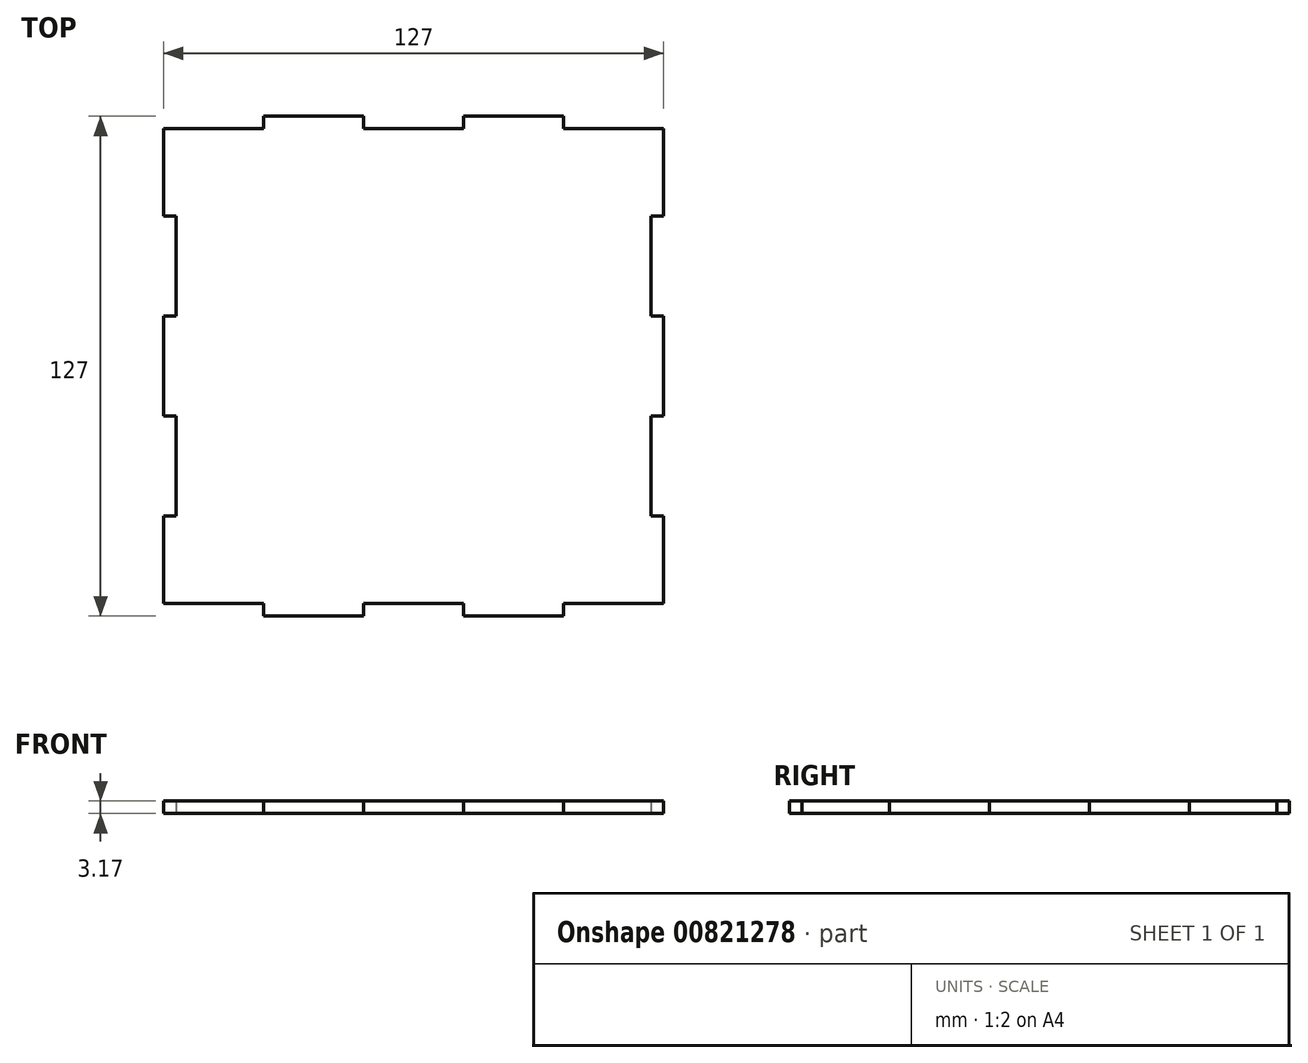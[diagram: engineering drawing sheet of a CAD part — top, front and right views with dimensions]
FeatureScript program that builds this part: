
annotation { "Feature Type Name" : "Feature", "Feature Type Description" : "" }
export const myFeature = defineFeature(function(context is Context, id is Id, definition is map)
    precondition{}
    {
        {
            var Q0;
            Q0=qCreatedBy(makeId("Top.planeOp"),FACE);
            var sketch = newSketch(context, id + "F0", { "sketchPlane" : qUnion([Q0])});
            skLineSegment(sketch, "E0.bottom", {"start": v(-63.5, 63.5) * mm, "end": v(63.5, 63.5) * mm});
            skLineSegment(sketch, "E0.top", {"start": v(-63.5, -63.5) * mm, "end": v(63.5, -63.5) * mm});
            skLineSegment(sketch, "E0.left", {"start": v(-63.5, 63.5) * mm, "end": v(-63.5, -63.5) * mm});
            skLineSegment(sketch, "E0.right", {"start": v(63.5, 63.5) * mm, "end": v(63.5, -63.5) * mm});
            skPoint(sketch, "E0.middle", {"position": v(0, 0) * mm});
            skLineSegment(sketch, "E1", {"start": v(-38.1, 63.5) * mm, "end": v(-38.1, -63.5) * mm});
            skLineSegment(sketch, "E2", {"start": v(-63.5, -38.1) * mm, "end": v(63.5, -38.1) * mm});
            skLineSegment(sketch, "E3.1.0.0", {"start": v(-12.7, 63.5) * mm, "end": v(-12.7, -63.5) * mm});
            skLineSegment(sketch, "E3.2.0.0", {"start": v(12.7, 63.5) * mm, "end": v(12.7, -63.5) * mm});
            skLineSegment(sketch, "E3.3.0.0", {"start": v(38.1, 63.5) * mm, "end": v(38.1, -63.5) * mm});
            skLineSegment(sketch, "E3.direction1", {"start": v(-38.1, -63.5) * mm, "end": v(-12.7, -63.5) * mm, "construction": true});
            skLineSegment(sketch, "E4.0.1.0", {"start": v(-63.5, -12.7) * mm, "end": v(63.5, -12.7) * mm});
            skLineSegment(sketch, "E4.0.2.0", {"start": v(-63.5, 12.7) * mm, "end": v(63.5, 12.7) * mm});
            skLineSegment(sketch, "E4.0.3.0", {"start": v(-63.5, 38.1) * mm, "end": v(63.5, 38.1) * mm});
            skLineSegment(sketch, "E4.1.0.0", {"start": v(-38.1, -38.1) * mm, "end": v(63.5, -38.1) * mm});
            skLineSegment(sketch, "E4.1.1.0", {"start": v(-38.1, -12.7) * mm, "end": v(63.5, -12.7) * mm});
            skLineSegment(sketch, "E4.1.2.0", {"start": v(-38.1, 12.7) * mm, "end": v(63.5, 12.7) * mm});
            skLineSegment(sketch, "E4.1.3.0", {"start": v(-38.1, 38.1) * mm, "end": v(63.5, 38.1) * mm});
            skLineSegment(sketch, "E4.2.0.0", {"start": v(-12.7, -38.1) * mm, "end": v(63.5, -38.1) * mm});
            skLineSegment(sketch, "E4.2.1.0", {"start": v(-12.7, -12.7) * mm, "end": v(63.5, -12.7) * mm});
            skLineSegment(sketch, "E4.2.2.0", {"start": v(-12.7, 12.7) * mm, "end": v(63.5, 12.7) * mm});
            skLineSegment(sketch, "E4.2.3.0", {"start": v(-12.7, 38.1) * mm, "end": v(63.5, 38.1) * mm});
            skLineSegment(sketch, "E4.direction1", {"start": v(-63.5, -38.1) * mm, "end": v(-38.1, -38.1) * mm, "construction": true});
            skLineSegment(sketch, "E4.direction2", {"start": v(-63.5, -38.1) * mm, "end": v(-63.5, -12.7) * mm, "construction": true});
            skLineSegment(sketch, "E5", {"start": v(-63.5, -60.33) * mm, "end": v(63.5, -60.32) * mm});
            skLineSegment(sketch, "E6", {"start": v(-60.33, 63.5) * mm, "end": v(-60.33, -63.5) * mm});
            skLineSegment(sketch, "E7", {"start": v(-63.5, 60.33) * mm, "end": v(63.5, 60.33) * mm});
            skLineSegment(sketch, "E8", {"start": v(60.32, 63.5) * mm, "end": v(60.32, -63.5) * mm});
            skSolve(sketch);
        }
        {
            var Q0;
            {var subQ0=sQuery(id+"F0.wireOp",EDGE,"E7");var subQ1=sQuery(id+"F0.wireOp",EDGE,"E1");var subQ2=makeQuery(id+"F0.imprint","INTERSECT",VERTEX,{"derivedFrom":[subQ1,subQ0]});Q0=makeQuery(id+"F0.imprint","IMPRINT",FACE,{"disambiguationData":[TD([[makeQuery(id+"F0.imprint","IMPRINT",EDGE,{"disambiguationData":[TD([[subQ2,-1.0]])],"derivedFrom":subQ1}),-1.0]])]});}
            var Q1;
            {var subQ0=sQuery(id+"F0.wireOp",EDGE,"E7");var subQ1=sQuery(id+"F0.wireOp",EDGE,"E1");var subQ2=makeQuery(id+"F0.imprint","INTERSECT",VERTEX,{"derivedFrom":[subQ1,subQ0]});Q1=makeQuery(id+"F0.imprint","IMPRINT",FACE,{"disambiguationData":[TD([[makeQuery(id+"F0.imprint","IMPRINT",EDGE,{"disambiguationData":[TD([[subQ2,-1.0]])],"derivedFrom":subQ1}),1.0]])]});}
            var Q2;
            {var subQ0=sQuery(id+"F0.wireOp",EDGE,"E7");var subQ1=sQuery(id+"F0.wireOp",EDGE,"E3.2.0.0");var subQ2=makeQuery(id+"F0.imprint","INTERSECT",VERTEX,{"derivedFrom":[subQ1,subQ0]});Q2=makeQuery(id+"F0.imprint","IMPRINT",FACE,{"disambiguationData":[TD([[makeQuery(id+"F0.imprint","IMPRINT",EDGE,{"disambiguationData":[TD([[subQ2,-1.0]])],"derivedFrom":subQ1}),1.0]])]});}
            var Q3;
            {var subQ0=sQuery(id+"F0.wireOp",EDGE,"E7");var subQ1=sQuery(id+"F0.wireOp",EDGE,"E3.3.0.0");var subQ2=makeQuery(id+"F0.imprint","INTERSECT",VERTEX,{"derivedFrom":[subQ1,subQ0]});Q3=makeQuery(id+"F0.imprint","IMPRINT",FACE,{"disambiguationData":[TD([[makeQuery(id+"F0.imprint","IMPRINT",EDGE,{"disambiguationData":[TD([[subQ2,-1.0]])],"derivedFrom":subQ1}),1.0]])]});}
            var Q4;
            {var subQ0=sQuery(id+"F0.wireOp",EDGE,"E4.0.2.0");var subQ1=sQuery(id+"F0.wireOp",EDGE,"E3.3.0.0");var subQ2=makeQuery(id+"F0.imprint","INTERSECT",VERTEX,{"derivedFrom":[subQ1,subQ0]});Q4=makeQuery(id+"F0.imprint","IMPRINT",FACE,{"disambiguationData":[TD([[makeQuery(id+"F0.imprint","IMPRINT",EDGE,{"disambiguationData":[TD([[subQ2,1.0]])],"derivedFrom":subQ1}),1.0]])]});}
            var Q5;
            {var subQ0=sQuery(id+"F0.wireOp",EDGE,"E4.0.2.0");var subQ1=sQuery(id+"F0.wireOp",EDGE,"E3.2.0.0");var subQ2=makeQuery(id+"F0.imprint","INTERSECT",VERTEX,{"derivedFrom":[subQ1,subQ0]});Q5=makeQuery(id+"F0.imprint","IMPRINT",FACE,{"disambiguationData":[TD([[makeQuery(id+"F0.imprint","IMPRINT",EDGE,{"disambiguationData":[TD([[subQ2,1.0]])],"derivedFrom":subQ1}),1.0]])]});}
            var Q6;
            {var subQ0=sQuery(id+"F0.wireOp",EDGE,"E4.0.2.0");var subQ1=sQuery(id+"F0.wireOp",EDGE,"E3.1.0.0");var subQ2=makeQuery(id+"F0.imprint","INTERSECT",VERTEX,{"derivedFrom":[subQ1,subQ0]});Q6=makeQuery(id+"F0.imprint","IMPRINT",FACE,{"disambiguationData":[TD([[makeQuery(id+"F0.imprint","IMPRINT",EDGE,{"disambiguationData":[TD([[subQ2,1.0]])],"derivedFrom":subQ1}),1.0]])]});}
            var Q7;
            {var subQ0=sQuery(id+"F0.wireOp",EDGE,"E4.0.2.0");var subQ1=sQuery(id+"F0.wireOp",EDGE,"E1");var subQ2=makeQuery(id+"F0.imprint","INTERSECT",VERTEX,{"derivedFrom":[subQ1,subQ0]});Q7=makeQuery(id+"F0.imprint","IMPRINT",FACE,{"disambiguationData":[TD([[makeQuery(id+"F0.imprint","IMPRINT",EDGE,{"disambiguationData":[TD([[subQ2,1.0]])],"derivedFrom":subQ1}),1.0]])]});}
            var Q8;
            {var subQ0=sQuery(id+"F0.wireOp",EDGE,"E4.0.2.0");var subQ1=sQuery(id+"F0.wireOp",EDGE,"E1");var subQ2=makeQuery(id+"F0.imprint","INTERSECT",VERTEX,{"derivedFrom":[subQ1,subQ0]});Q8=makeQuery(id+"F0.imprint","IMPRINT",FACE,{"disambiguationData":[TD([[makeQuery(id+"F0.imprint","IMPRINT",EDGE,{"disambiguationData":[TD([[subQ2,1.0]])],"derivedFrom":subQ1}),-1.0]])]});}
            var Q9;
            {var subQ0=sQuery(id+"F0.wireOp",EDGE,"E4.0.2.0");var subQ1=sQuery(id+"F0.wireOp",EDGE,"E1");var subQ2=makeQuery(id+"F0.imprint","INTERSECT",VERTEX,{"derivedFrom":[subQ1,subQ0]});Q9=makeQuery(id+"F0.imprint","IMPRINT",FACE,{"disambiguationData":[TD([[makeQuery(id+"F0.imprint","IMPRINT",EDGE,{"disambiguationData":[TD([[subQ2,-1.0]])],"derivedFrom":subQ1}),-1.0]])]});}
            var Q10;
            {var subQ0=sQuery(id+"F0.wireOp",EDGE,"E4.0.2.0");var subQ1=sQuery(id+"F0.wireOp",EDGE,"E1");var subQ2=makeQuery(id+"F0.imprint","INTERSECT",VERTEX,{"derivedFrom":[subQ1,subQ0]});Q10=makeQuery(id+"F0.imprint","IMPRINT",FACE,{"disambiguationData":[TD([[makeQuery(id+"F0.imprint","IMPRINT",EDGE,{"disambiguationData":[TD([[subQ2,-1.0]])],"derivedFrom":subQ1}),1.0]])]});}
            var Q11;
            {var subQ0=sQuery(id+"F0.wireOp",EDGE,"E4.0.1.0");var subQ1=sQuery(id+"F0.wireOp",EDGE,"E3.1.0.0");var subQ2=makeQuery(id+"F0.imprint","INTERSECT",VERTEX,{"derivedFrom":[subQ1,subQ0]});Q11=makeQuery(id+"F0.imprint","IMPRINT",FACE,{"disambiguationData":[TD([[makeQuery(id+"F0.imprint","IMPRINT",EDGE,{"disambiguationData":[TD([[subQ2,1.0]])],"derivedFrom":subQ1}),1.0]])]});}
            var Q12;
            {var subQ0=sQuery(id+"F0.wireOp",EDGE,"E4.0.1.0");var subQ1=sQuery(id+"F0.wireOp",EDGE,"E3.2.0.0");var subQ2=makeQuery(id+"F0.imprint","INTERSECT",VERTEX,{"derivedFrom":[subQ1,subQ0]});Q12=makeQuery(id+"F0.imprint","IMPRINT",FACE,{"disambiguationData":[TD([[makeQuery(id+"F0.imprint","IMPRINT",EDGE,{"disambiguationData":[TD([[subQ2,1.0]])],"derivedFrom":subQ1}),1.0]])]});}
            var Q13;
            {var subQ0=sQuery(id+"F0.wireOp",EDGE,"E4.0.1.0");var subQ1=sQuery(id+"F0.wireOp",EDGE,"E3.3.0.0");var subQ2=makeQuery(id+"F0.imprint","INTERSECT",VERTEX,{"derivedFrom":[subQ1,subQ0]});Q13=makeQuery(id+"F0.imprint","IMPRINT",FACE,{"disambiguationData":[TD([[makeQuery(id+"F0.imprint","IMPRINT",EDGE,{"disambiguationData":[TD([[subQ2,1.0]])],"derivedFrom":subQ1}),1.0]])]});}
            var Q14;
            {var subQ0=sQuery(id+"F0.wireOp",EDGE,"E3.3.0.0");var subQ1=sQuery(id+"F0.wireOp",EDGE,"E2");var subQ2=makeQuery(id+"F0.imprint","INTERSECT",VERTEX,{"derivedFrom":[subQ1,subQ0]});Q14=makeQuery(id+"F0.imprint","IMPRINT",FACE,{"disambiguationData":[TD([[makeQuery(id+"F0.imprint","IMPRINT",EDGE,{"disambiguationData":[TD([[subQ2,-1.0]])],"derivedFrom":subQ1}),1.0]])]});}
            var Q15;
            {var subQ0=sQuery(id+"F0.wireOp",EDGE,"E3.2.0.0");var subQ1=sQuery(id+"F0.wireOp",EDGE,"E2");var subQ2=makeQuery(id+"F0.imprint","INTERSECT",VERTEX,{"derivedFrom":[subQ1,subQ0]});Q15=makeQuery(id+"F0.imprint","IMPRINT",FACE,{"disambiguationData":[TD([[makeQuery(id+"F0.imprint","IMPRINT",EDGE,{"disambiguationData":[TD([[subQ2,-1.0]])],"derivedFrom":subQ1}),1.0]])]});}
            var Q16;
            {var subQ0=sQuery(id+"F0.wireOp",EDGE,"E3.1.0.0");var subQ1=sQuery(id+"F0.wireOp",EDGE,"E2");var subQ2=makeQuery(id+"F0.imprint","INTERSECT",VERTEX,{"derivedFrom":[subQ1,subQ0]});Q16=makeQuery(id+"F0.imprint","IMPRINT",FACE,{"disambiguationData":[TD([[makeQuery(id+"F0.imprint","IMPRINT",EDGE,{"disambiguationData":[TD([[subQ2,-1.0]])],"derivedFrom":subQ1}),1.0]])]});}
            var Q17;
            {var subQ0=sQuery(id+"F0.wireOp",EDGE,"E4.0.1.0");var subQ1=sQuery(id+"F0.wireOp",EDGE,"E1");var subQ2=makeQuery(id+"F0.imprint","INTERSECT",VERTEX,{"derivedFrom":[subQ1,subQ0]});Q17=makeQuery(id+"F0.imprint","IMPRINT",FACE,{"disambiguationData":[TD([[makeQuery(id+"F0.imprint","IMPRINT",EDGE,{"disambiguationData":[TD([[subQ2,-1.0]])],"derivedFrom":subQ1}),1.0]])]});}
            var Q18;
            {var subQ0=sQuery(id+"F0.wireOp",EDGE,"E4.0.1.0");var subQ1=sQuery(id+"F0.wireOp",EDGE,"E1");var subQ2=makeQuery(id+"F0.imprint","INTERSECT",VERTEX,{"derivedFrom":[subQ1,subQ0]});Q18=makeQuery(id+"F0.imprint","IMPRINT",FACE,{"disambiguationData":[TD([[makeQuery(id+"F0.imprint","IMPRINT",EDGE,{"disambiguationData":[TD([[subQ2,-1.0]])],"derivedFrom":subQ1}),-1.0]])]});}
            var Q19;
            {var subQ0=sQuery(id+"F0.wireOp",EDGE,"E5");var subQ1=sQuery(id+"F0.wireOp",EDGE,"E1");var subQ2=makeQuery(id+"F0.imprint","INTERSECT",VERTEX,{"derivedFrom":[subQ1,subQ0]});Q19=makeQuery(id+"F0.imprint","IMPRINT",FACE,{"disambiguationData":[TD([[makeQuery(id+"F0.imprint","IMPRINT",EDGE,{"disambiguationData":[TD([[subQ2,1.0]])],"derivedFrom":subQ1}),-1.0]])]});}
            var Q20;
            {var subQ0=sQuery(id+"F0.wireOp",EDGE,"E5");var subQ1=sQuery(id+"F0.wireOp",EDGE,"E1");var subQ2=makeQuery(id+"F0.imprint","INTERSECT",VERTEX,{"derivedFrom":[subQ1,subQ0]});Q20=makeQuery(id+"F0.imprint","IMPRINT",FACE,{"disambiguationData":[TD([[makeQuery(id+"F0.imprint","IMPRINT",EDGE,{"disambiguationData":[TD([[subQ2,1.0]])],"derivedFrom":subQ1}),1.0]])]});}
            var Q21;
            {var subQ0=sQuery(id+"F0.wireOp",EDGE,"E3.2.0.0");var subQ1=sQuery(id+"F0.wireOp",EDGE,"E2");var subQ2=makeQuery(id+"F0.imprint","INTERSECT",VERTEX,{"derivedFrom":[subQ1,subQ0]});Q21=makeQuery(id+"F0.imprint","IMPRINT",FACE,{"disambiguationData":[TD([[makeQuery(id+"F0.imprint","IMPRINT",EDGE,{"disambiguationData":[TD([[subQ2,-1.0]])],"derivedFrom":subQ1}),-1.0]])]});}
            var Q22;
            {var subQ0=sQuery(id+"F0.wireOp",EDGE,"E3.3.0.0");var subQ1=sQuery(id+"F0.wireOp",EDGE,"E2");var subQ2=makeQuery(id+"F0.imprint","INTERSECT",VERTEX,{"derivedFrom":[subQ1,subQ0]});Q22=makeQuery(id+"F0.imprint","IMPRINT",FACE,{"disambiguationData":[TD([[makeQuery(id+"F0.imprint","IMPRINT",EDGE,{"disambiguationData":[TD([[subQ2,-1.0]])],"derivedFrom":subQ1}),-1.0]])]});}
            var Q23;
            {var subQ0=sQuery(id+"F0.wireOp",EDGE,"E7");var subQ1=sQuery(id+"F0.wireOp",EDGE,"E3.1.0.0");var subQ2=makeQuery(id+"F0.imprint","INTERSECT",VERTEX,{"derivedFrom":[subQ1,subQ0]});Q23=makeQuery(id+"F0.imprint","IMPRINT",FACE,{"disambiguationData":[TD([[makeQuery(id+"F0.imprint","IMPRINT",EDGE,{"disambiguationData":[TD([[subQ2,-1.0]])],"derivedFrom":subQ1}),1.0]])]});}
            var Q24;
            {var subQ0=sQuery(id+"F0.wireOp",EDGE,"E3.1.0.0");var subQ1=sQuery(id+"F0.wireOp",EDGE,"E2");var subQ2=makeQuery(id+"F0.imprint","INTERSECT",VERTEX,{"derivedFrom":[subQ1,subQ0]});Q24=makeQuery(id+"F0.imprint","IMPRINT",FACE,{"disambiguationData":[TD([[makeQuery(id+"F0.imprint","IMPRINT",EDGE,{"disambiguationData":[TD([[subQ2,-1.0]])],"derivedFrom":subQ1}),-1.0]])]});}
            var Q25;
            {var subQ0=sQuery(id+"F0.wireOp",EDGE,"E2");var subQ1=sQuery(id+"F0.wireOp",EDGE,"E0.left");var subQ2=makeQuery(id+"F0.imprint","INTERSECT",VERTEX,{"derivedFrom":[subQ1,subQ0]});Q25=makeQuery(id+"F0.imprint","IMPRINT",FACE,{"disambiguationData":[TD([[makeQuery(id+"F0.imprint","IMPRINT",EDGE,{"disambiguationData":[TD([[subQ2,-1.0]])],"derivedFrom":subQ1}),1.0]])]});}
            var Q26;
            {var subQ0=sQuery(id+"F0.wireOp",EDGE,"E4.0.2.0");var subQ1=sQuery(id+"F0.wireOp",EDGE,"E0.left");var subQ2=makeQuery(id+"F0.imprint","INTERSECT",VERTEX,{"derivedFrom":[subQ1,subQ0]});Q26=makeQuery(id+"F0.imprint","IMPRINT",FACE,{"disambiguationData":[TD([[makeQuery(id+"F0.imprint","IMPRINT",EDGE,{"disambiguationData":[TD([[subQ2,-1.0]])],"derivedFrom":subQ1}),1.0]])]});}
            var Q27;
            {var subQ0=sQuery(id+"F0.wireOp",EDGE,"E7");var subQ1=sQuery(id+"F0.wireOp",EDGE,"E0.left");var subQ2=makeQuery(id+"F0.imprint","INTERSECT",VERTEX,{"derivedFrom":[subQ1,subQ0]});Q27=makeQuery(id+"F0.imprint","IMPRINT",FACE,{"disambiguationData":[TD([[makeQuery(id+"F0.imprint","IMPRINT",EDGE,{"disambiguationData":[TD([[subQ2,-1.0]])],"derivedFrom":subQ1}),1.0]])]});}
            var Q28;
            {var subQ0=sQuery(id+"F0.wireOp",EDGE,"E7");var subQ1=sQuery(id+"F0.wireOp",EDGE,"E0.right");var subQ2=makeQuery(id+"F0.imprint","INTERSECT",VERTEX,{"derivedFrom":[subQ1,subQ0]});Q28=makeQuery(id+"F0.imprint","IMPRINT",FACE,{"disambiguationData":[TD([[makeQuery(id+"F0.imprint","IMPRINT",EDGE,{"disambiguationData":[TD([[subQ2,-1.0]])],"derivedFrom":subQ1}),-1.0]])]});}
            var Q29;
            {var subQ0=sQuery(id+"F0.wireOp",EDGE,"E4.0.2.0");var subQ1=sQuery(id+"F0.wireOp",EDGE,"E0.right");var subQ2=makeQuery(id+"F0.imprint","INTERSECT",VERTEX,{"derivedFrom":[subQ1,subQ0]});Q29=makeQuery(id+"F0.imprint","IMPRINT",FACE,{"disambiguationData":[TD([[makeQuery(id+"F0.imprint","IMPRINT",EDGE,{"disambiguationData":[TD([[subQ2,-1.0]])],"derivedFrom":subQ1}),-1.0]])]});}
            var Q30;
            {var subQ0=sQuery(id+"F0.wireOp",EDGE,"E5");var subQ1=sQuery(id+"F0.wireOp",EDGE,"E0.right");var subQ2=makeQuery(id+"F0.imprint","INTERSECT",VERTEX,{"derivedFrom":[subQ1,subQ0]});Q30=makeQuery(id+"F0.imprint","IMPRINT",FACE,{"disambiguationData":[TD([[makeQuery(id+"F0.imprint","IMPRINT",EDGE,{"disambiguationData":[TD([[subQ2,1.0]])],"derivedFrom":subQ1}),-1.0]])]});}
            var Q31;
            {var subQ0=sQuery(id+"F0.wireOp",EDGE,"E3.1.0.0");var subQ1=sQuery(id+"F0.wireOp",EDGE,"E0.top");var subQ2=makeQuery(id+"F0.imprint","INTERSECT",VERTEX,{"derivedFrom":[subQ1,subQ0]});Q31=makeQuery(id+"F0.imprint","IMPRINT",FACE,{"disambiguationData":[TD([[makeQuery(id+"F0.imprint","IMPRINT",EDGE,{"disambiguationData":[TD([[subQ2,1.0]])],"derivedFrom":subQ1}),1.0]])]});}
            var Q32;
            {var subQ0=sQuery(id+"F0.wireOp",EDGE,"E3.2.0.0");var subQ1=sQuery(id+"F0.wireOp",EDGE,"E0.top");var subQ2=makeQuery(id+"F0.imprint","INTERSECT",VERTEX,{"derivedFrom":[subQ1,subQ0]});Q32=makeQuery(id+"F0.imprint","IMPRINT",FACE,{"disambiguationData":[TD([[makeQuery(id+"F0.imprint","IMPRINT",EDGE,{"disambiguationData":[TD([[subQ2,-1.0]])],"derivedFrom":subQ1}),1.0]])]});}
            var Q33;
            {var subQ0=sQuery(id+"F0.wireOp",EDGE,"E1");var subQ1=sQuery(id+"F0.wireOp",EDGE,"E0.bottom");var subQ2=makeQuery(id+"F0.imprint","INTERSECT",VERTEX,{"derivedFrom":[subQ1,subQ0]});Q33=makeQuery(id+"F0.imprint","IMPRINT",FACE,{"disambiguationData":[TD([[makeQuery(id+"F0.imprint","IMPRINT",EDGE,{"disambiguationData":[TD([[subQ2,-1.0]])],"derivedFrom":subQ1}),-1.0]])]});}
            var Q34;
            {var subQ0=sQuery(id+"F0.wireOp",EDGE,"E3.2.0.0");var subQ1=sQuery(id+"F0.wireOp",EDGE,"E0.bottom");var subQ2=makeQuery(id+"F0.imprint","INTERSECT",VERTEX,{"derivedFrom":[subQ1,subQ0]});Q34=makeQuery(id+"F0.imprint","IMPRINT",FACE,{"disambiguationData":[TD([[makeQuery(id+"F0.imprint","IMPRINT",EDGE,{"disambiguationData":[TD([[subQ2,-1.0]])],"derivedFrom":subQ1}),-1.0]])]});}
            extrude(context, id + "F1", {"entities" : qUnion([Q0, Q1, Q2, Q3, Q4, Q5, Q6, Q7, Q8, Q9, Q10, Q11, Q12, Q13, Q14, Q15, Q16, Q17, Q18, Q19, Q20, Q21, Q22, Q23, Q24, Q25, Q26, Q27, Q28, Q29, Q30, Q31, Q32, Q33, Q34]), "depth" : 3.17 * mm, "offsetDistance" : 25.4 * mm});
        }
    });
